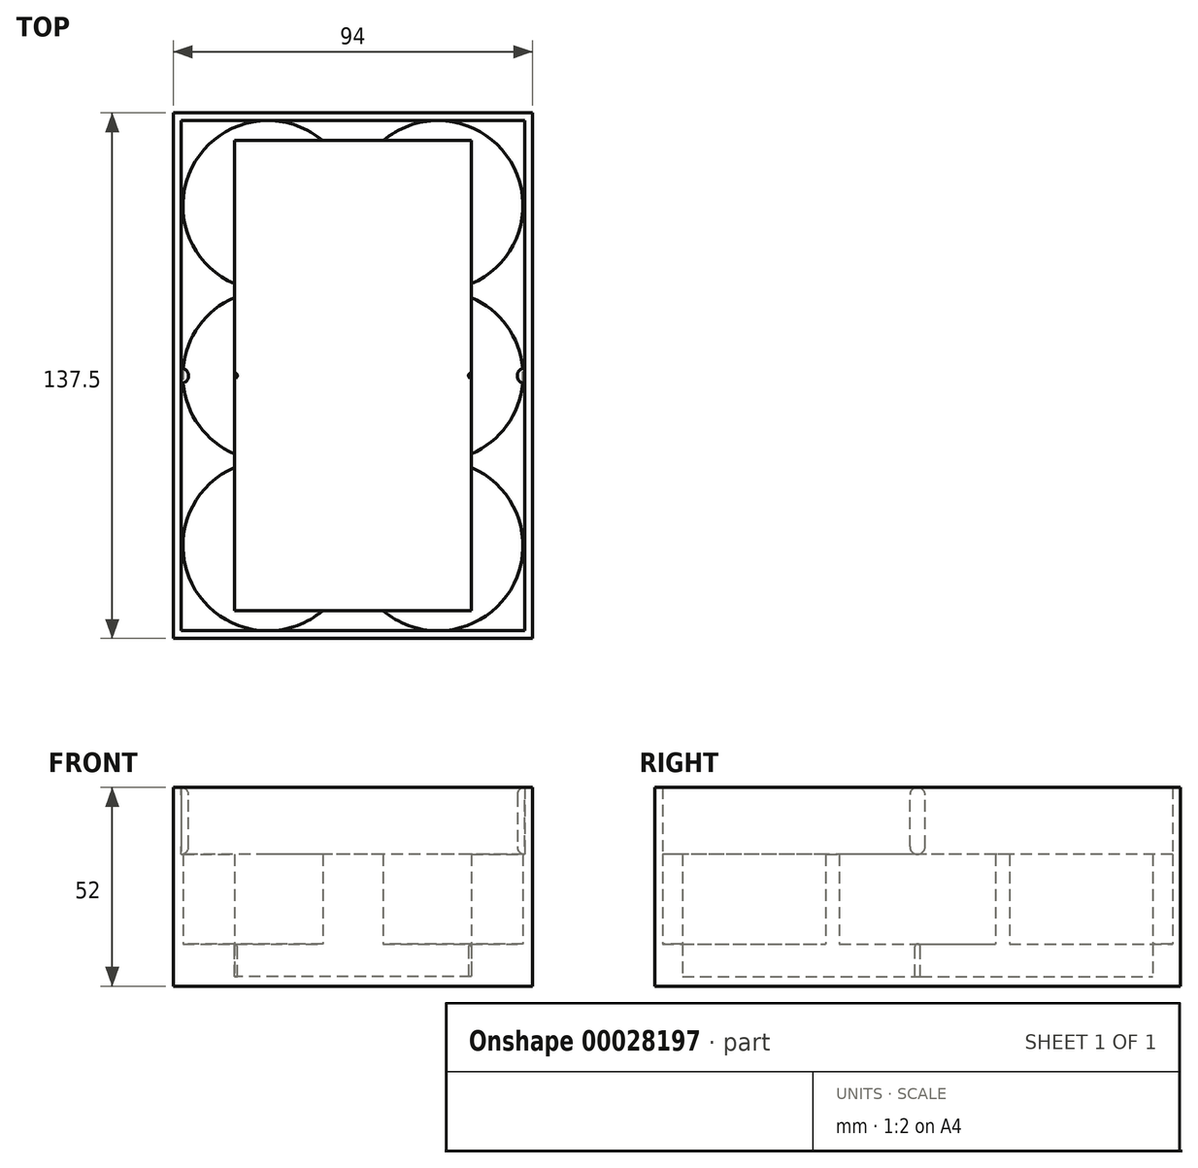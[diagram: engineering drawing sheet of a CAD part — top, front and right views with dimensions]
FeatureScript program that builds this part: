
annotation { "Feature Type Name" : "Feature", "Feature Type Description" : "" }
export const myFeature = defineFeature(function(context is Context, id is Id, definition is map)
    precondition{}
    {
        {
            var Q0;
            Q0=qCreatedBy(makeId("Top.planeOp"),FACE);
            var sketch = newSketch(context, id + "F0", { "sketchPlane" : qUnion([Q0])});
            skLineSegment(sketch, "E0.rect.bottom", {"start": v(47, 68.75) * mm, "end": v(-47, 68.75) * mm});
            skLineSegment(sketch, "E0.rect.top", {"start": v(47, -68.75) * mm, "end": v(-47, -68.75) * mm});
            skLineSegment(sketch, "E0.rect.left", {"start": v(47, 68.75) * mm, "end": v(47, -68.75) * mm});
            skLineSegment(sketch, "E0.rect.right", {"start": v(-47, 68.75) * mm, "end": v(-47, -68.75) * mm});
            skPoint(sketch, "E0.rect.middle", {"position": v(0, 0) * mm});
            skSolve(sketch);
        }
        {
            var Q0;
            Q0 = qSketchRegion(id + "F0", true);
            extrude(context, id + "F1", {"entities" : qUnion([Q0]), "depth" : 2.5 * mm});
        }
        {
            var Q0;
            Q0=makeQuery(id+"F1.opExtrude","CAP_FACE",FACE,{"disambiguationData":[OSD([sQuery(id+"F0.wireOp",EDGE,"E0.rect.bottom"),sQuery(id+"F0.wireOp",EDGE,"E0.rect.top"),sQuery(id+"F0.wireOp",EDGE,"E0.rect.left"),sQuery(id+"F0.wireOp",EDGE,"E0.rect.right")])],"isStart":false});
            var sketch = newSketch(context, id + "F2", { "sketchPlane" : qUnion([Q0])});
            skLineSegment(sketch, "E1.rect.bottom", {"start": v(47, 68.75) * mm, "end": v(-47, 68.75) * mm});
            skLineSegment(sketch, "E1.rect.top", {"start": v(47, -68.75) * mm, "end": v(-47, -68.75) * mm});
            skLineSegment(sketch, "E1.rect.left", {"start": v(47, 68.75) * mm, "end": v(47, -68.75) * mm});
            skLineSegment(sketch, "E1.rect.right", {"start": v(-47, 68.75) * mm, "end": v(-47, -68.75) * mm});
            skPoint(sketch, "E1.rect.middle", {"position": v(0, 0) * mm});
            skLineSegment(sketch, "E2.rect.bottom", {"start": v(31, -61.5) * mm, "end": v(-31, -61.5) * mm});
            skLineSegment(sketch, "E2.rect.top", {"start": v(31, 61.5) * mm, "end": v(-31, 61.5) * mm});
            skLineSegment(sketch, "E2.rect.left", {"start": v(31, -61.5) * mm, "end": v(31, 61.5) * mm});
            skLineSegment(sketch, "E2.rect.right", {"start": v(-31, -61.5) * mm, "end": v(-31, 61.5) * mm});
            skSolve(sketch);
        }
        {
            var Q0;
            Q0 = qSketchRegion(id + "F2", true);
            extrude(context, id + "F3", {"entities" : qUnion([Q0]), "operationType" : NewBodyOperationType.ADD, "depth" : 8.5 * mm});
        }
        {
            var Q0;
            Q0=makeQuery(id+"F3.opExtrude","CAP_FACE",FACE,{"disambiguationData":[OSD([sQuery(id+"F2.wireOp",EDGE,"E1.rect.bottom"),sQuery(id+"F2.wireOp",EDGE,"E1.rect.top"),sQuery(id+"F2.wireOp",EDGE,"E1.rect.left"),sQuery(id+"F2.wireOp",EDGE,"E1.rect.right"),sQuery(id+"F2.wireOp",EDGE,"E2.rect.bottom"),sQuery(id+"F2.wireOp",EDGE,"E2.rect.top"),sQuery(id+"F2.wireOp",EDGE,"E2.rect.left"),sQuery(id+"F2.wireOp",EDGE,"E2.rect.right")])],"isStart":false});
            var sketch = newSketch(context, id + "F4", { "sketchPlane" : qUnion([Q0])});
            skPoint(sketch, "E3.rect.middle", {"position": v(0, 0) * mm});
            skCircle(sketch, "E4", {"center": v(-22.25, 44.5) * mm, "radius": 22.25 * mm});
            skCircle(sketch, "E5", {"center": v(-22.25, -44.5) * mm, "radius": 22.25 * mm});
            skCircle(sketch, "E6", {"center": v(22.25, -44.5) * mm, "radius": 22.25 * mm});
            skCircle(sketch, "E7", {"center": v(22.25, 0) * mm, "radius": 22.25 * mm});
            skCircle(sketch, "E8", {"center": v(-22.25, 0) * mm, "radius": 22.25 * mm});
            skCircle(sketch, "E9", {"center": v(22.25, 44.5) * mm, "radius": 22.25 * mm});
            skLineSegment(sketch, "E10.rect.bottom", {"start": v(47, -68.75) * mm, "end": v(-47, -68.75) * mm});
            skLineSegment(sketch, "E10.rect.top", {"start": v(47, 68.75) * mm, "end": v(-47, 68.75) * mm});
            skLineSegment(sketch, "E10.rect.left", {"start": v(47, -68.75) * mm, "end": v(47, 68.75) * mm});
            skLineSegment(sketch, "E10.rect.right", {"start": v(-47, -68.75) * mm, "end": v(-47, 68.75) * mm});
            skLineSegment(sketch, "E11", {"start": v(-22.25, 44.5) * mm, "end": v(22.25, 44.5) * mm});
            skLineSegment(sketch, "E12", {"start": v(-22.25, 0) * mm, "end": v(22.25, 0) * mm});
            skLineSegment(sketch, "E13", {"start": v(-22.25, -44.5) * mm, "end": v(22.25, -44.5) * mm});
            skSolve(sketch);
        }
        {
            var Q0;
            Q0 = qSketchRegion(id + "F4", true);
            extrude(context, id + "F5", {"entities" : qUnion([Q0]), "operationType" : NewBodyOperationType.ADD, "depth" : 23.5 * mm});
        }
        {
            var Q0;
            {var subQ0=sQuery(id+"F2.wireOp",EDGE,"E2.rect.top");var subQ1=sQuery(id+"F2.wireOp",EDGE,"E2.rect.right");var subQ2=sQuery(id+"F4.wireOp",EDGE,"E4");Q0=makeQuery(id+"F5.boolean.opBoolean","SPLIT",FACE,{"disambiguationData":[TD([makeQuery(id+"F5.opExtrude","SWEPT_FACE",FACE,{"disambiguationData":[OSD([subQ2])]})])],"derivedFrom":makeQuery(id+"F3.opExtrude","CAP_FACE",FACE,{"disambiguationData":[OSD([sQuery(id+"F2.wireOp",EDGE,"E1.rect.bottom"),sQuery(id+"F2.wireOp",EDGE,"E1.rect.top"),sQuery(id+"F2.wireOp",EDGE,"E1.rect.left"),sQuery(id+"F2.wireOp",EDGE,"E1.rect.right"),sQuery(id+"F2.wireOp",EDGE,"E2.rect.bottom"),subQ0,sQuery(id+"F2.wireOp",EDGE,"E2.rect.left"),subQ1])],"isStart":false})});}
            var sketch = newSketch(context, id + "F6", { "sketchPlane" : qUnion([Q0])});
            skLineSegment(sketch, "E14.rect.bottom", {"start": v(-31, 61.5) * mm, "end": v(31, 61.5) * mm});
            skLineSegment(sketch, "E14.rect.top", {"start": v(-31, -61.5) * mm, "end": v(31, -61.5) * mm});
            skLineSegment(sketch, "E14.rect.left", {"start": v(-31, 61.5) * mm, "end": v(-31, -61.5) * mm});
            skLineSegment(sketch, "E14.rect.right", {"start": v(31, 61.5) * mm, "end": v(31, -61.5) * mm});
            skPoint(sketch, "E14.rect.middle", {"position": v(0, 0) * mm});
            skSolve(sketch);
        }
        {
            var Q0;
            Q0 = qSketchRegion(id + "F6", true);
            extrude(context, id + "F7", {"entities" : qUnion([Q0]), "operationType" : NewBodyOperationType.REMOVE, "endBound" : BoundingType.THROUGH_ALL, "depth" : 25 * mm});
        }
        {
            var Q0;
            Q0=makeQuery(id+"F5.opExtrude","CAP_FACE",FACE,{"disambiguationData":[OSD([sQuery(id+"F4.wireOp",EDGE,"E4"),sQuery(id+"F4.wireOp",EDGE,"E5"),sQuery(id+"F4.wireOp",EDGE,"E6"),sQuery(id+"F4.wireOp",EDGE,"E7"),sQuery(id+"F4.wireOp",EDGE,"E8"),sQuery(id+"F4.wireOp",EDGE,"E9"),sQuery(id+"F4.wireOp",EDGE,"E10.rect.bottom"),sQuery(id+"F4.wireOp",EDGE,"E10.rect.top"),sQuery(id+"F4.wireOp",EDGE,"E10.rect.left"),sQuery(id+"F4.wireOp",EDGE,"E10.rect.right")])],"isStart":false});
            var sketch = newSketch(context, id + "F8", { "sketchPlane" : qUnion([Q0])});
            skLineSegment(sketch, "E15.rect.bottom", {"start": v(47, 68.75) * mm, "end": v(-47, 68.75) * mm});
            skLineSegment(sketch, "E15.rect.top", {"start": v(47, -68.75) * mm, "end": v(-47, -68.75) * mm});
            skLineSegment(sketch, "E15.rect.left", {"start": v(47, 68.75) * mm, "end": v(47, -68.75) * mm});
            skLineSegment(sketch, "E15.rect.right", {"start": v(-47, 68.75) * mm, "end": v(-47, -68.75) * mm});
            skPoint(sketch, "E15.rect.middle", {"position": v(0, 0) * mm});
            skLineSegment(sketch, "E16.rect.bottom", {"start": v(45, 66.75) * mm, "end": v(-45, 66.75) * mm});
            skLineSegment(sketch, "E16.rect.top", {"start": v(45, -66.75) * mm, "end": v(-45, -66.75) * mm});
            skLineSegment(sketch, "E16.rect.left", {"start": v(45, 66.75) * mm, "end": v(45, -66.75) * mm});
            skLineSegment(sketch, "E16.rect.right", {"start": v(-45, 66.75) * mm, "end": v(-45, -66.75) * mm});
            skSolve(sketch);
        }
        {
            var Q0;
            Q0 = qSketchRegion(id + "F8", true);
            extrude(context, id + "F9", {"entities" : qUnion([Q0]), "operationType" : NewBodyOperationType.ADD, "depth" : 17.5 * mm});
        }
        {
            var Q0;
            Q0=makeQuery(id+"F9.opExtrude","SWEPT_FACE",FACE,{"disambiguationData":[OSD([sQuery(id+"F8.wireOp",EDGE,"E16.rect.right")])]});
            var sketch = newSketch(context, id + "F10", { "sketchPlane" : qUnion([Q0])});
            skLineSegment(sketch, "E17", {"start": v(0, 34.5) * mm, "end": v(0, 52) * mm});
            skLineSegment(sketch, "E18", {"start": v(0, 52) * mm, "end": v(0, 50) * mm});
            skLineSegment(sketch, "E19", {"start": v(0, 34.5) * mm, "end": v(0, 36.5) * mm});
            skLineSegment(sketch, "E20", {"start": v(2, 50) * mm, "end": v(2, 36.5) * mm});
            skLineSegment(sketch, "E21", {"start": v(0, 52) * mm, "end": v(0, 34.5) * mm});
            skArc(sketch, "E22", {"start": v(2, 50) * mm, "mid": v(1.41, 51.41) * mm, "end": v(0, 52) * mm});
            skArc(sketch, "E23", {"start": v(0, 34.5) * mm, "mid": v(1.41, 35.09) * mm, "end": v(2, 36.5) * mm});
            skSolve(sketch);
        }
        {
            var Q0;
            Q0 = qSketchRegion(id + "F10", true);
            var Q1;
            Q1=sQuery(id+"F10.wireOp",EDGE,"E21");
            revolve(context, id + "F11", {"operationType" : NewBodyOperationType.ADD, "entities" : qUnion([Q0]), "axis" : qUnion([Q1]), "revolveType" : RevolveType.ONE_DIRECTION, "angle" : 180 * degree});
        }
        {
            var Q0;
            Q0=makeQuery(id+"F9.opExtrude","SWEPT_FACE",FACE,{"disambiguationData":[OSD([sQuery(id+"F8.wireOp",EDGE,"E16.rect.left")])]});
            var sketch = newSketch(context, id + "F12", { "sketchPlane" : qUnion([Q0])});
            skLineSegment(sketch, "E24", {"start": v(0, 34.5) * mm, "end": v(0, 52) * mm});
            skLineSegment(sketch, "E25", {"start": v(0, 34.5) * mm, "end": v(0, 36.5) * mm});
            skLineSegment(sketch, "E26", {"start": v(0, 52) * mm, "end": v(0, 50) * mm});
            skLineSegment(sketch, "E27", {"start": v(-2, 36.5) * mm, "end": v(-2, 50) * mm});
            skLineSegment(sketch, "E28", {"start": v(0, 50) * mm, "end": v(-2, 50) * mm});
            skArc(sketch, "E29", {"start": v(0, 52) * mm, "mid": v(-1.41, 51.41) * mm, "end": v(-2, 50) * mm});
            skArc(sketch, "E30", {"start": v(-2, 36.5) * mm, "mid": v(-1.41, 35.09) * mm, "end": v(0, 34.5) * mm});
            skSolve(sketch);
        }
        {
            var Q0;
            Q0 = qSketchRegion(id + "F12", true);
            var Q1;
            Q1=sQuery(id+"F12.wireOp",EDGE,"E24");
            revolve(context, id + "F13", {"operationType" : NewBodyOperationType.ADD, "entities" : qUnion([Q0]), "axis" : qUnion([Q1]), "revolveType" : RevolveType.ONE_DIRECTION, "angle" : 180 * degree});
        }
        {
            var Q0;
            Q0=makeQuery(id+"F7.boolean.opBoolean","MERGE",FACE,{"derivedFrom":[makeQuery(id+"F3.opExtrude","SWEPT_FACE",FACE,{"disambiguationData":[OSD([sQuery(id+"F2.wireOp",EDGE,"E2.rect.right")])]}),makeQuery(id+"F7.opExtrude","SWEPT_FACE",FACE,{"disambiguationData":[OSD([sQuery(id+"F6.wireOp",EDGE,"E14.rect.left")])]})]});
            var sketch = newSketch(context, id + "F14", { "sketchPlane" : qUnion([Q0])});
            skLineSegment(sketch, "E31", {"start": v(0, 11) * mm, "end": v(0, 2.5) * mm});
            skLineSegment(sketch, "E32", {"start": v(0, 2.5) * mm, "end": v(0.75, 2.5) * mm});
            skLineSegment(sketch, "E33", {"start": v(0, 11) * mm, "end": v(0, 10.25) * mm});
            skLineSegment(sketch, "E34", {"start": v(0, 10.25) * mm, "end": v(0.75, 10.25) * mm});
            skArc(sketch, "E35", {"start": v(0.75, 10.25) * mm, "mid": v(0.53, 10.78) * mm, "end": v(0, 11) * mm});
            skLineSegment(sketch, "E36", {"start": v(0.75, 10.25) * mm, "end": v(0.75, 2.5) * mm});
            skSolve(sketch);
        }
        {
            var Q0;
            Q0 = qSketchRegion(id + "F14", true);
            var Q1;
            Q1=sQuery(id+"F14.wireOp",EDGE,"E31");
            revolve(context, id + "F15", {"operationType" : NewBodyOperationType.ADD, "entities" : qUnion([Q0]), "axis" : qUnion([Q1]), "revolveType" : RevolveType.FULL});
        }
        {
            var Q0;
            Q0=makeQuery(id+"F7.boolean.opBoolean","MERGE",FACE,{"derivedFrom":[makeQuery(id+"F3.opExtrude","SWEPT_FACE",FACE,{"disambiguationData":[OSD([sQuery(id+"F2.wireOp",EDGE,"E2.rect.left")])]}),makeQuery(id+"F7.opExtrude","SWEPT_FACE",FACE,{"disambiguationData":[OSD([sQuery(id+"F6.wireOp",EDGE,"E14.rect.right")])]})]});
            var sketch = newSketch(context, id + "F16", { "sketchPlane" : qUnion([Q0])});
            skLineSegment(sketch, "E37", {"start": v(0, 2.5) * mm, "end": v(0, 11) * mm});
            skLineSegment(sketch, "E38", {"start": v(0, 2.5) * mm, "end": v(-0.75, 2.5) * mm});
            skLineSegment(sketch, "E39", {"start": v(0, 11) * mm, "end": v(0, 10.25) * mm});
            skLineSegment(sketch, "E40", {"start": v(0, 10.25) * mm, "end": v(-0.75, 10.25) * mm});
            skArc(sketch, "E41", {"start": v(0, 11) * mm, "mid": v(-0.53, 10.78) * mm, "end": v(-0.75, 10.25) * mm});
            skLineSegment(sketch, "E42", {"start": v(-0.75, 2.5) * mm, "end": v(-0.75, 10.25) * mm});
            skSolve(sketch);
        }
        {
            var Q0;
            Q0 = qSketchRegion(id + "F16", true);
            var Q1;
            Q1=sQuery(id+"F16.wireOp",EDGE,"E37");
            revolve(context, id + "F17", {"operationType" : NewBodyOperationType.ADD, "entities" : qUnion([Q0]), "axis" : qUnion([Q1]), "revolveType" : RevolveType.FULL});
        }
    });
